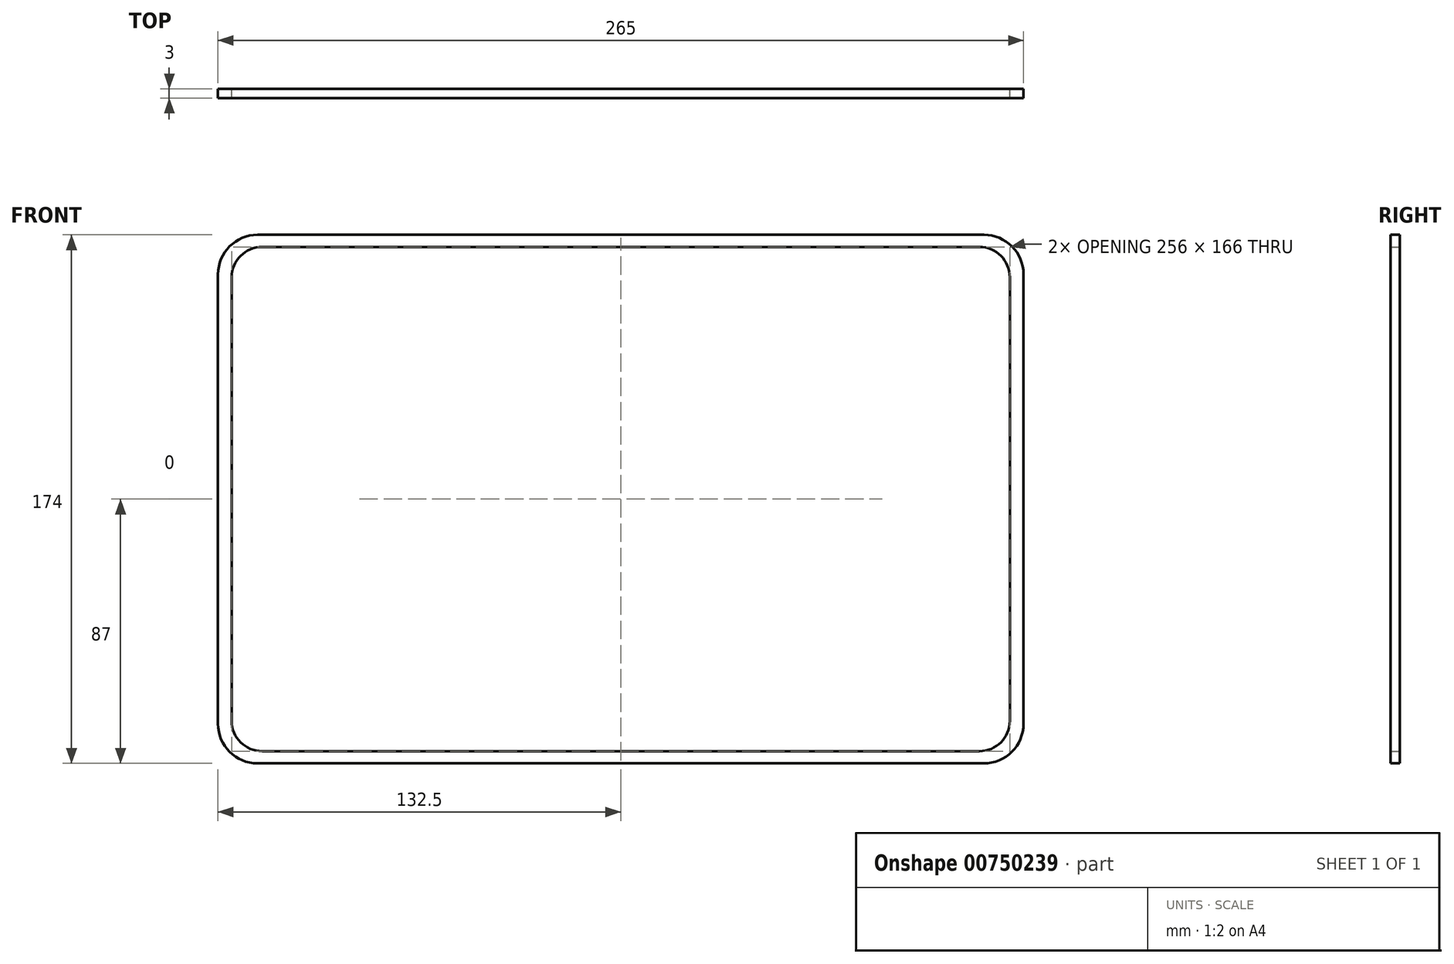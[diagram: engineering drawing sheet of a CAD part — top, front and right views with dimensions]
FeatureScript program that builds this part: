
annotation { "Feature Type Name" : "Feature", "Feature Type Description" : "" }
export const myFeature = defineFeature(function(context is Context, id is Id, definition is map)
    precondition{}
    {
        {
            var Q0;
            Q0=qCreatedBy(makeId("Front.planeOp"),FACE);
            var sketch = newSketch(context, id + "F0", { "sketchPlane" : qUnion([Q0])});
            skLineSegment(sketch, "E0.bottom", {"start": v(119.5, -87) * mm, "end": v(-119.5, -87) * mm});
            skLineSegment(sketch, "E0.top", {"start": v(119.5, 87) * mm, "end": v(-119.5, 87) * mm});
            skLineSegment(sketch, "E0.left", {"start": v(132.5, -74) * mm, "end": v(132.5, 74) * mm});
            skLineSegment(sketch, "E0.right", {"start": v(-132.5, -74) * mm, "end": v(-132.5, 74) * mm});
            skPoint(sketch, "E0.middle", {"position": v(0, 0) * mm});
            skLineSegment(sketch, "E1.bottom", {"start": v(118, -83) * mm, "end": v(-118, -83) * mm});
            skLineSegment(sketch, "E1.top", {"start": v(118, 83) * mm, "end": v(-118, 83) * mm});
            skLineSegment(sketch, "E1.left", {"start": v(128, -73) * mm, "end": v(128, 73) * mm});
            skLineSegment(sketch, "E1.right", {"start": v(-128, -73) * mm, "end": v(-128, 73) * mm});
            skPoint(sketch, "E2.visualSharp", {"position": v(-128, 83) * mm});
            skArc(sketch, "E2.filletArc", {"start": v(-118, 83) * mm, "mid": v(-125.07, 80.07) * mm, "end": v(-128, 73) * mm});
            skPoint(sketch, "E3.visualSharp", {"position": v(128, 83) * mm});
            skArc(sketch, "E3.filletArc", {"start": v(128, 73) * mm, "mid": v(125.07, 80.07) * mm, "end": v(118, 83) * mm});
            skPoint(sketch, "E4.visualSharp", {"position": v(-128, -83) * mm});
            skArc(sketch, "E4.filletArc", {"start": v(-128, -73) * mm, "mid": v(-125.07, -80.07) * mm, "end": v(-118, -83) * mm});
            skPoint(sketch, "E5.visualSharp", {"position": v(128, -83) * mm});
            skArc(sketch, "E5.filletArc", {"start": v(118, -83) * mm, "mid": v(125.07, -80.07) * mm, "end": v(128, -73) * mm});
            skPoint(sketch, "E6.visualSharp", {"position": v(-132.5, 87) * mm});
            skArc(sketch, "E6.filletArc", {"start": v(-119.5, 87) * mm, "mid": v(-128.7, 83.2) * mm, "end": v(-132.5, 74) * mm});
            skPoint(sketch, "E7.visualSharp", {"position": v(-132.5, -87) * mm});
            skArc(sketch, "E7.filletArc", {"start": v(-132.5, -74) * mm, "mid": v(-128.7, -83.2) * mm, "end": v(-119.5, -87) * mm});
            skPoint(sketch, "E8.visualSharp", {"position": v(132.5, -87) * mm});
            skArc(sketch, "E8.filletArc", {"start": v(119.5, -87) * mm, "mid": v(128.7, -83.2) * mm, "end": v(132.5, -74) * mm});
            skPoint(sketch, "E9.visualSharp", {"position": v(132.5, 87) * mm});
            skArc(sketch, "E9.filletArc", {"start": v(132.5, 74) * mm, "mid": v(128.7, 83.2) * mm, "end": v(119.5, 87) * mm});
            skSolve(sketch);
        }
        {
            var Q0;
            Q0=makeQuery(id+"F0.imprint","IMPRINT",FACE,{"disambiguationData":[TD([[makeQuery(id+"F0.imprint","IMPRINT",EDGE,{"derivedFrom":sQuery(id+"F0.wireOp",EDGE,"E0.bottom")}),-1.0]])]});
            extrude(context, id + "F1", {"entities" : qUnion([Q0]), "depth" : 3 * mm, "offsetDistance" : 25 * mm});
        }
    });
